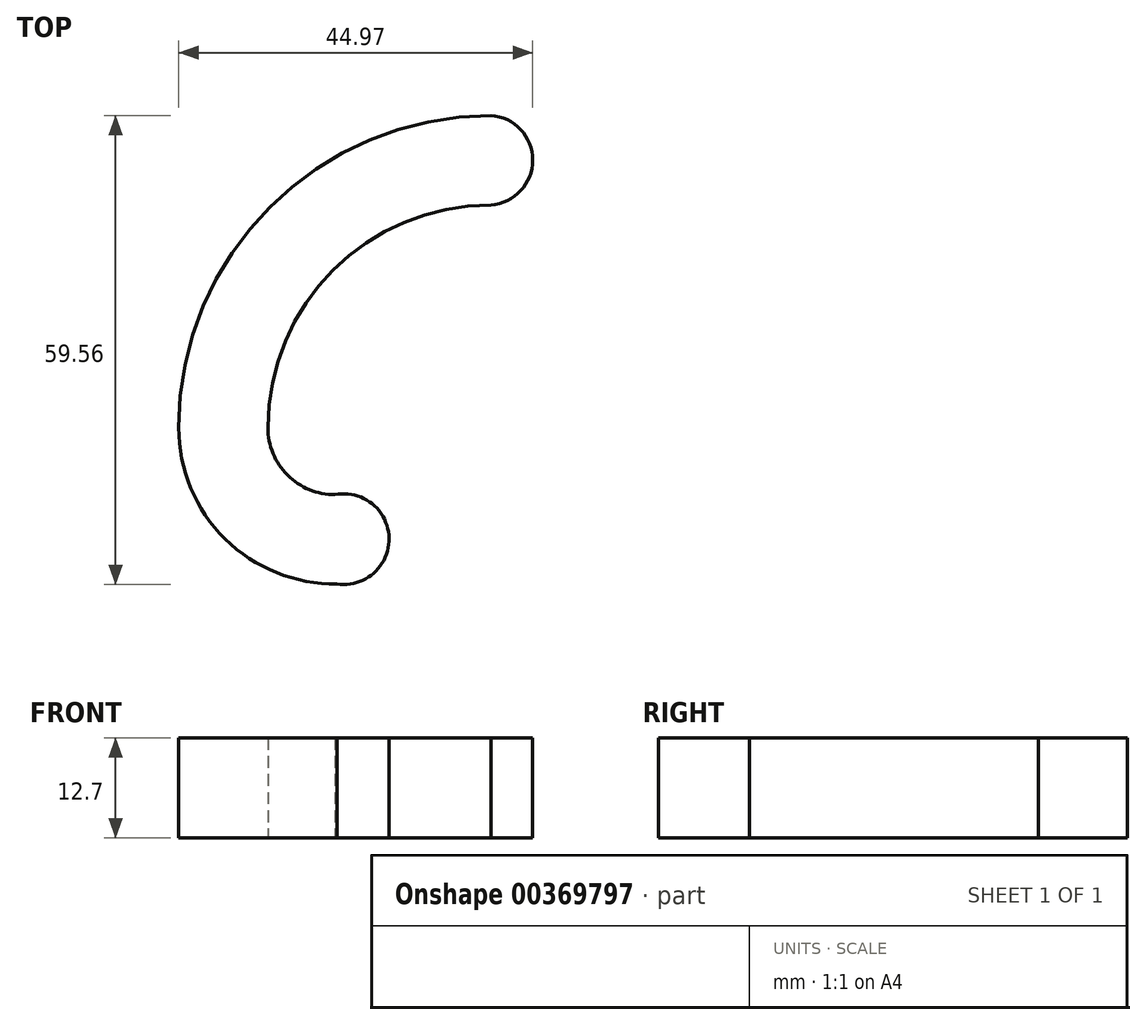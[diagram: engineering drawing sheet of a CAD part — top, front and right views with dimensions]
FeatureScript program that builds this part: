
annotation { "Feature Type Name" : "Feature", "Feature Type Description" : "" }
export const myFeature = defineFeature(function(context is Context, id is Id, definition is map)
    precondition{}
    {
        {
            var Q0;
            Q0=qCreatedBy(makeId("Top.planeOp"),FACE);
            var sketch = newSketch(context, id + "F0", { "sketchPlane" : qUnion([Q0])});
            skArc(sketch, "E0", {"start": v(0, 28.32) * mm, "mid": v(-20.02, 20.02) * mm, "end": v(-28.32, 0) * mm});
            skArc(sketch, "E1", {"start": v(0, 28.32) * mm, "mid": v(-0.43, 28.31) * mm, "end": v(-0.86, 28.3) * mm});
            skArc(sketch, "E2", {"start": v(0, 39.65) * mm, "mid": v(-28.04, 28.04) * mm, "end": v(-39.65, 0) * mm});
            skArc(sketch, "E3", {"start": v(-28.32, 0) * mm, "mid": v(-25.82, -6.02) * mm, "end": v(-19.8, -8.5) * mm});
            skArc(sketch, "E4", {"start": v(-39.65, 0) * mm, "mid": v(-33.75, -14.12) * mm, "end": v(-19.55, -19.84) * mm});
            skArc(sketch, "E5", {"start": v(-19.55, -19.84) * mm, "mid": v(-12.93, -14.03) * mm, "end": v(-19.8, -8.5) * mm});
            skArc(sketch, "E6", {"start": v(0, 28.32) * mm, "mid": v(5.32, 33.98) * mm, "end": v(0, 39.65) * mm});
            skSolve(sketch);
        }
        {
            var Q0;
            Q0=makeQuery(id+"F0.imprint","IMPRINT",FACE,{"disambiguationData":[TD([[makeQuery(id+"F0.imprint","IMPRINT",EDGE,{"derivedFrom":sQuery(id+"F0.wireOp",EDGE,"E0")}),-1.0]])]});
            extrude(context, id + "F1", {"entities" : qUnion([Q0]), "depth" : 12.7 * mm});
        }
    });
